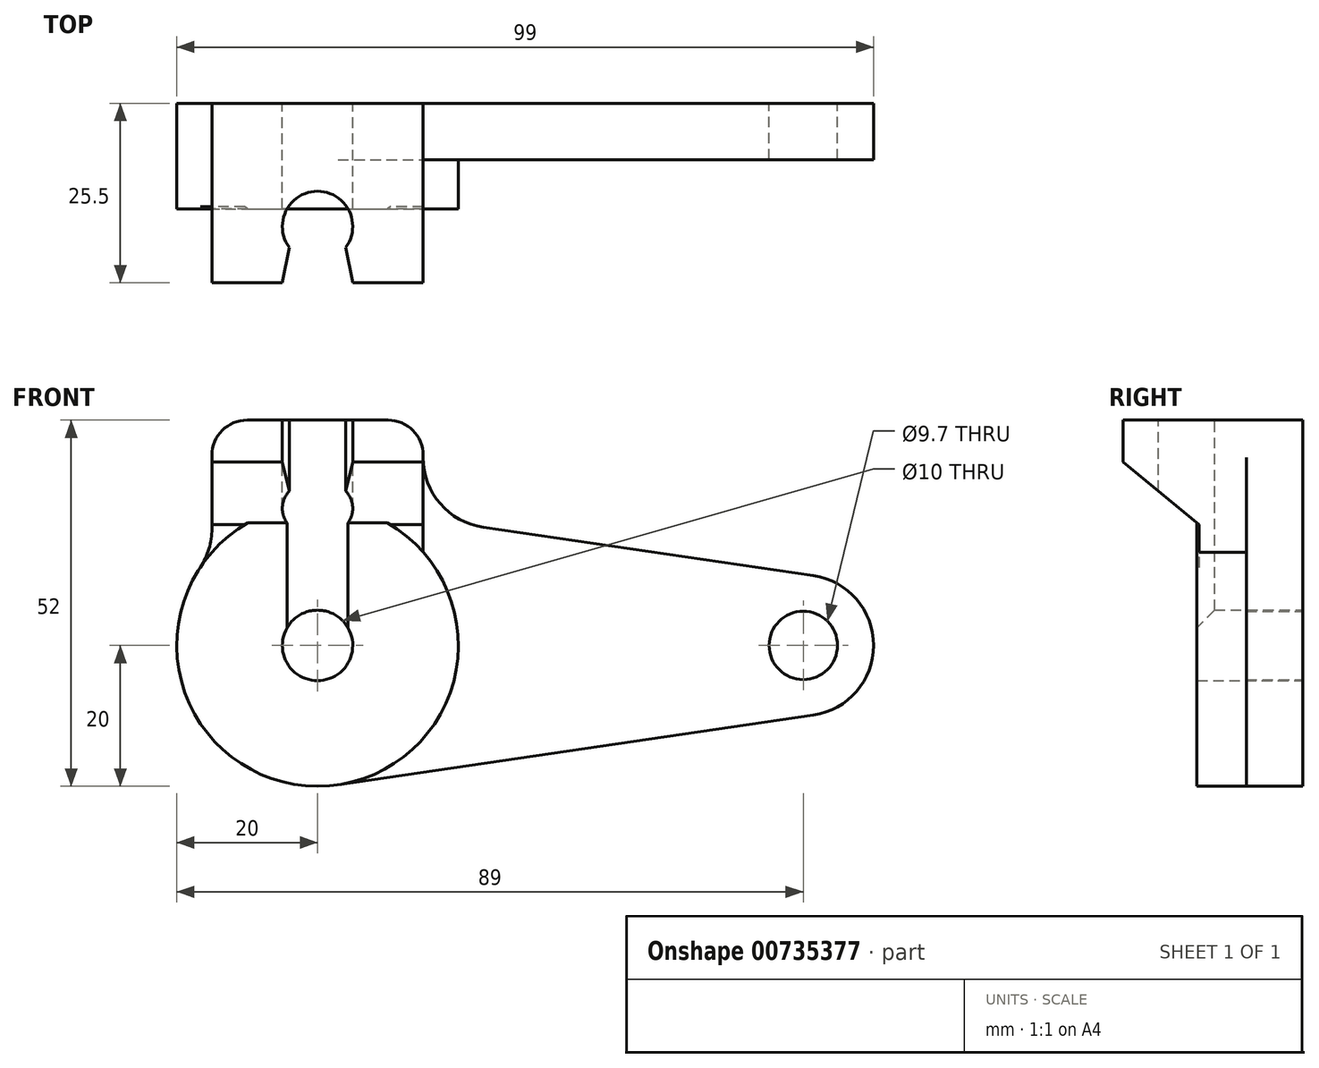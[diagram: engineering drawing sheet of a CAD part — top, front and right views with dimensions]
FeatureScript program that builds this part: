
annotation { "Feature Type Name" : "Feature", "Feature Type Description" : "" }
export const myFeature = defineFeature(function(context is Context, id is Id, definition is map)
    precondition{}
    {
        {
            var Q0;
            Q0=qCreatedBy(makeId("Front.planeOp"),FACE);
            var sketch = newSketch(context, id + "F0", { "sketchPlane" : qUnion([Q0])});
            skCircle(sketch, "E0", {"center": v(0, 0) * mm, "radius": 20 * mm});
            skCircle(sketch, "E1", {"center": v(69, 0) * mm, "radius": 10 * mm});
            skLineSegment(sketch, "E2", {"start": v(2.9, 19.79) * mm, "end": v(70.45, 9.9) * mm});
            skLineSegment(sketch, "E3", {"start": v(2.9, -19.79) * mm, "end": v(70.45, -9.9) * mm});
            skSolve(sketch);
        }
        {
            var Q0;
            {var subQ0=sQuery(id+"F0.wireOp",EDGE,"E0");var subQ1=makeQuery(id+"F0.imprint","INTERSECT",VERTEX,{"derivedFrom":[subQ0,sQuery(id+"F0.wireOp",EDGE,"E2")]});Q0=makeQuery(id+"F0.imprint","IMPRINT",FACE,{"disambiguationData":[TD([[makeQuery(id+"F0.imprint","IMPRINT",EDGE,{"disambiguationData":[TD([[subQ1,-1.0]])],"derivedFrom":subQ0}),1.0]])]});}
            extrude(context, id + "F1", {"entities" : qUnion([Q0]), "depth" : 15 * mm, "offsetDistance" : 25 * mm});
        }
        {
            var Q0;
            {var subQ0=sQuery(id+"F0.wireOp",EDGE,"E2");Q0=makeQuery(id+"F0.imprint","IMPRINT",FACE,{"disambiguationData":[TD([[makeQuery(id+"F0.imprint","IMPRINT",EDGE,{"derivedFrom":subQ0}),-1.0]])]});}
            var Q1;
            {var subQ0=sQuery(id+"F0.wireOp",EDGE,"E1");var subQ1=makeQuery(id+"F0.imprint","INTERSECT",VERTEX,{"derivedFrom":[subQ0,sQuery(id+"F0.wireOp",EDGE,"E2")]});Q1=makeQuery(id+"F0.imprint","IMPRINT",FACE,{"disambiguationData":[TD([[makeQuery(id+"F0.imprint","IMPRINT",EDGE,{"disambiguationData":[TD([[subQ1,-1.0]])],"derivedFrom":subQ0}),1.0]])]});}
            extrude(context, id + "F2", {"entities" : qUnion([Q0, Q1]), "operationType" : NewBodyOperationType.ADD, "depth" : 8 * mm, "offsetDistance" : 25 * mm});
        }
        {
            var Q0;
            Q0=qCreatedBy(makeId("Right.planeOp"),FACE);
            var sketch = newSketch(context, id + "F3", { "sketchPlane" : qUnion([Q0])});
            skLineSegment(sketch, "E4", {"start": v(0, 0) * mm, "end": v(-14.7, 0) * mm});
            skLineSegment(sketch, "E5", {"start": v(-14.7, 0) * mm, "end": v(-14.7, 17.14) * mm});
            skLineSegment(sketch, "E6", {"start": v(-14.7, 17.14) * mm, "end": v(-25.5, 26.05) * mm});
            skLineSegment(sketch, "E7", {"start": v(-25.5, 26.05) * mm, "end": v(-25.5, 32) * mm});
            skLineSegment(sketch, "E8", {"start": v(-25.5, 32) * mm, "end": v(0, 32) * mm});
            skLineSegment(sketch, "E9", {"start": v(0, 32) * mm, "end": v(0, 0) * mm});
            skSolve(sketch);
        }
        {
            var Q0;
            Q0=makeQuery(id+"F3.imprint","IMPRINT",FACE,{"disambiguationData":[TD([[makeQuery(id+"F3.imprint","IMPRINT",EDGE,{"derivedFrom":sQuery(id+"F3.wireOp",EDGE,"E4")}),-1.0]])]});
            extrude(context, id + "F4", {"entities" : qUnion([Q0]), "operationType" : NewBodyOperationType.ADD, "depth" : 30 * mm, "offsetDistance" : 25 * mm, "symmetric" : true});
        }
        {
            var Q0;
            Q0=sQuery(id+"F0.wireOp",VERTEX,"E1.center");
            var Q1;
            Q1=makeQuery(id+"F1.opExtrude","SWEPT_BODY",BODY,{"disambiguationData":[OSD([sQuery(id+"F0.wireOp",EDGE,"E0")])]});
            hole(context, id + "F5", {"style" : HoleStyle.SIMPLE, "endStyle" : HoleEndStyle.THROUGH, "oppositeDirection" : true, "holeDiameter" : 9.7 * mm, "majorDiameter" : 5 * mm, "isTappedThrough" : true, "tappedDepth" : 12 * mm, "tapClearance" : 3, "locations" : qUnion([Q0]), "scope" : qUnion([Q1])});
        }
        {
            var Q0;
            Q0=sQuery(id+"F0.wireOp",VERTEX,"E0.center");
            var Q1;
            Q1=makeQuery(id+"F1.opExtrude","SWEPT_BODY",BODY,{"disambiguationData":[OSD([sQuery(id+"F0.wireOp",EDGE,"E0")])]});
            hole(context, id + "F6", {"style" : HoleStyle.SIMPLE, "endStyle" : HoleEndStyle.THROUGH, "oppositeDirection" : true, "holeDiameter" : 10 * mm, "majorDiameter" : 5 * mm, "isTappedThrough" : true, "tappedDepth" : 12 * mm, "tapClearance" : 3, "locations" : qUnion([Q0]), "scope" : qUnion([Q1])});
        }
        {
            var Q0;
            Q0=makeQuery(id+"F4.opExtrude","SWEPT_FACE",FACE,{"disambiguationData":[OSD([sQuery(id+"F3.wireOp",EDGE,"E8")])]});
            var sketch = newSketch(context, id + "F7", { "sketchPlane" : qUnion([Q0])});
            skPoint(sketch, "E10", {"position": v(0, -17.5) * mm});
            skLineSegment(sketch, "E11", {"start": v(5, -25.5) * mm, "end": v(-5, -25.5) * mm});
            skArc(sketch, "E12", {"start": v(5, -17.5) * mm, "mid": v(0, -12.5) * mm, "end": v(-5, -17.5) * mm});
            skArc(sketch, "E13", {"start": v(-5, -17.5) * mm, "mid": v(-4.74, -19.08) * mm, "end": v(-4, -20.5) * mm});
            skArc(sketch, "E14", {"start": v(5, -17.5) * mm, "mid": v(4.74, -19.08) * mm, "end": v(4, -20.5) * mm});
            skLineSegment(sketch, "E15", {"start": v(-4, -20.5) * mm, "end": v(-5, -25.5) * mm});
            skLineSegment(sketch, "E16", {"start": v(4, -20.5) * mm, "end": v(5, -25.5) * mm});
            skSolve(sketch);
        }
        {
            var Q0;
            Q0 = qSketchRegion(id + "F7", true);
            extrude(context, id + "F8", {"entities" : qUnion([Q0]), "operationType" : NewBodyOperationType.REMOVE, "endBound" : BoundingType.UP_TO_NEXT, "oppositeDirection" : true, "depth" : 25 * mm, "offsetDistance" : 25 * mm});
        }
        {
            var Q0;
            Q0=makeQuery(id+"F4.opExtrude","CAP_EDGE",EDGE,{"disambiguationData":[OSD([sQuery(id+"F3.wireOp",EDGE,"E8")])],"isStart":false});
            var Q1;
            Q1=makeQuery(id+"F4.opExtrude","CAP_EDGE",EDGE,{"disambiguationData":[OSD([sQuery(id+"F3.wireOp",EDGE,"E8")])],"isStart":true});
            fillet(context, id + "F9", {"entities" : qUnion([Q0, Q1]), "radius" : 5 * mm, "tangentPropagation" : true, "allowEdgeOverflow" : false});
        }
        {
            var Q0;
            Q0=makeQuery(id+"F4.boolean.opBoolean","INTERSECT",EDGE,{"derivedFrom":[makeQuery(id+"F2.opExtrude","SWEPT_FACE",FACE,{"disambiguationData":[OSD([sQuery(id+"F0.wireOp",EDGE,"E2")])]}),makeQuery(id+"F4.opExtrude","CAP_FACE",FACE,{"disambiguationData":[OSD([sQuery(id+"F3.wireOp",EDGE,"E4"),sQuery(id+"F3.wireOp",EDGE,"E5"),sQuery(id+"F3.wireOp",EDGE,"E6"),sQuery(id+"F3.wireOp",EDGE,"E7"),sQuery(id+"F3.wireOp",EDGE,"E8"),sQuery(id+"F3.wireOp",EDGE,"E9")])],"isStart":false})]});
            var Q1;
            Q1=makeQuery(id+"F4.boolean.opBoolean","INTERSECT",EDGE,{"derivedFrom":[makeQuery(id+"F1.opExtrude","SWEPT_FACE",FACE,{"disambiguationData":[OSD([sQuery(id+"F0.wireOp",EDGE,"E0")])]}),makeQuery(id+"F4.opExtrude","CAP_FACE",FACE,{"disambiguationData":[OSD([sQuery(id+"F3.wireOp",EDGE,"E4"),sQuery(id+"F3.wireOp",EDGE,"E5"),sQuery(id+"F3.wireOp",EDGE,"E6"),sQuery(id+"F3.wireOp",EDGE,"E7"),sQuery(id+"F3.wireOp",EDGE,"E8"),sQuery(id+"F3.wireOp",EDGE,"E9")])],"isStart":true})]});
            fillet(context, id + "F10", {"entities" : qUnion([Q0, Q1]), "radius" : 10 * mm, "tangentPropagation" : true, "allowEdgeOverflow" : false});
        }
    });
